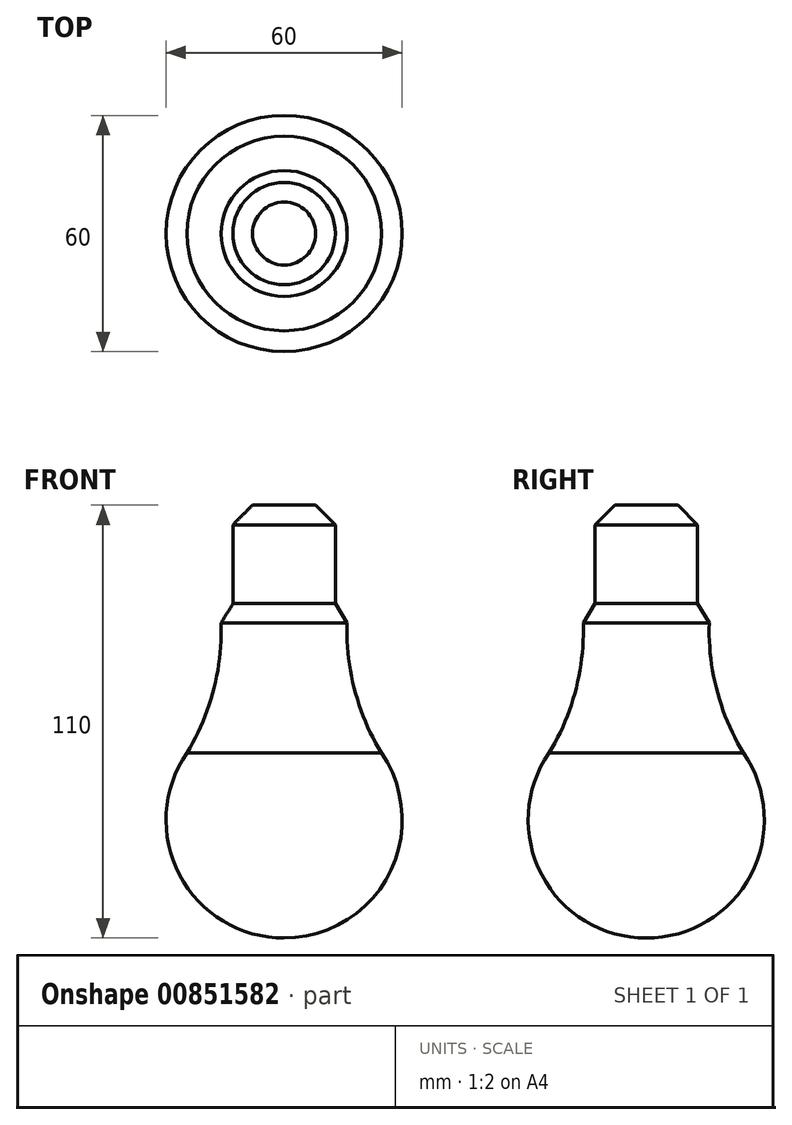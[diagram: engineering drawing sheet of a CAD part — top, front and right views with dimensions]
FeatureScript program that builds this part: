
annotation { "Feature Type Name" : "Feature", "Feature Type Description" : "" }
export const myFeature = defineFeature(function(context is Context, id is Id, definition is map)
    precondition{}
    {
        {
            var Q0;
            Q0=qCreatedBy(makeId("Front.planeOp"),FACE);
            var sketch = newSketch(context, id + "F0", { "sketchPlane" : qUnion([Q0])});
            skLineSegment(sketch, "E0", {"start": v(0, 144) * mm, "end": v(8, 144) * mm});
            skLineSegment(sketch, "E1", {"start": v(8, 144) * mm, "end": v(13, 139) * mm});
            skLineSegment(sketch, "E2", {"start": v(13, 139) * mm, "end": v(13, 119) * mm});
            skLineSegment(sketch, "E3", {"start": v(13, 119) * mm, "end": v(16, 114) * mm});
            skArc(sketch, "E4", {"start": v(0, 34) * mm, "mid": v(26.55, 50.04) * mm, "end": v(24.72, 81) * mm});
            skLineSegment(sketch, "E5", {"start": v(0, 34) * mm, "end": v(0, 144) * mm});
            skArc(sketch, "E6.filletArc", {"start": v(16, 114) * mm, "mid": v(17.96, 96.87) * mm, "end": v(24.72, 81) * mm});
            skSolve(sketch);
        }
        {
            var Q0;
            Q0=makeQuery(id+"F0.imprint","IMPRINT",FACE,{"disambiguationData":[TD([[makeQuery(id+"F0.imprint","IMPRINT",EDGE,{"derivedFrom":sQuery(id+"F0.wireOp",EDGE,"E0")}),-1.0]])]});
            var Q1;
            Q1=sQuery(id+"F0.wireOp",EDGE,"E5");
            revolve(context, id + "F1", {"surfaceOperationType" : NewSurfaceOperationType.NEW, "entities" : qUnion([Q0]), "axis" : qUnion([Q1]), "revolveType" : RevolveType.FULL});
        }
    });
